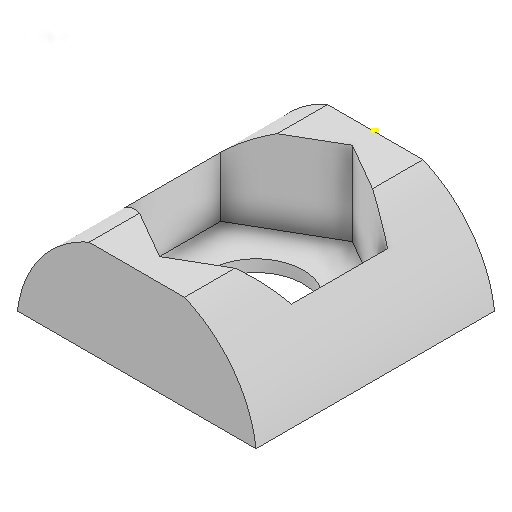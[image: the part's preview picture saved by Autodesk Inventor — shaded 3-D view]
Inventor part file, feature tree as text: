
AUTODESK INVENTOR PART (.ipt)
format: ipt  version: 2025.1 (Build 291241000, 241)  size: 134,144 bytes
history: native  units: mm
features: sketch x4, extrude x3
ambient origin geometry x8: Origin, YZ Plane, XZ Plane, XY Plane, X Axis, Y Axis, Z Axis, Center Point
bodies: Solid1 (feature_tree)
feature tree (7):
  extrude  "Extrusion1"  Depth=4.0mm
  extrude  "Extrusion2"  Depth=5.0mm
  sketch  "Sketch3"  dims[d4=5.0mm d5=10.0mm d6=0.0mm]
  extrude  "Extrusion4"  Depth=10.0mm TaperAngle=0.0deg
  sketch  "Sketch1"  dims[d0=10.0mm d1=4.0mm]
  sketch  "Sketch2"  dims[d2=4.0mm d3=5.0mm]
  sketch  "Sketch5"  dims[d7=3.95mm d8=5.0mm d9=2.0mm d10=10.0mm d11=0.0mm d15=3.5mm d16=3.5mm d17=0.0mm]
